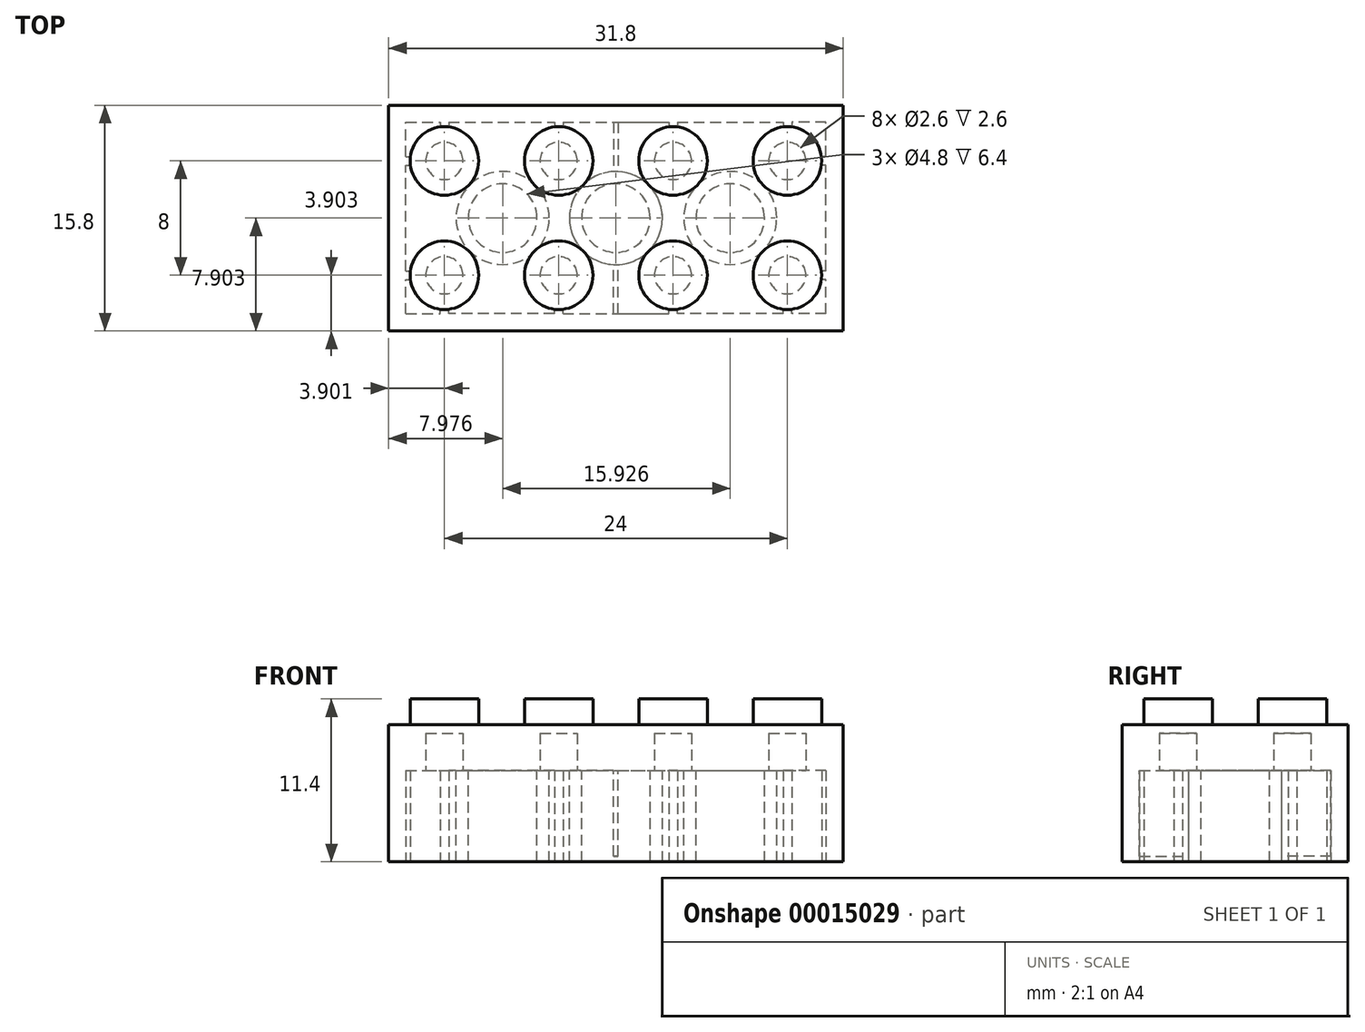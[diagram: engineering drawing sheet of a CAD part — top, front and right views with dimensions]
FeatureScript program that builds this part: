
annotation { "Feature Type Name" : "Feature", "Feature Type Description" : "" }
export const myFeature = defineFeature(function(context is Context, id is Id, definition is map)
    precondition{}
    {
        {
            var Q0;
            Q0=qCreatedBy(makeId("Top.planeOp"),FACE);
            var sketch = newSketch(context, id + "F0", { "sketchPlane" : qUnion([Q0])});
            skLineSegment(sketch, "E0.bottom", {"start": v(-8.05, -0.93) * mm, "end": v(23.75, -0.93) * mm});
            skLineSegment(sketch, "E0.top", {"start": v(-8.05, -16.73) * mm, "end": v(23.75, -16.73) * mm});
            skLineSegment(sketch, "E0.left", {"start": v(-8.05, -0.93) * mm, "end": v(-8.05, -16.73) * mm});
            skLineSegment(sketch, "E0.right", {"start": v(23.75, -0.93) * mm, "end": v(23.75, -16.73) * mm});
            skSolve(sketch);
        }
        {
            var Q0;
            Q0=qCreatedBy(makeId("Top.planeOp"),FACE);
            var sketch = newSketch(context, id + "F1", { "sketchPlane" : qUnion([Q0])});
            skCircle(sketch, "E1", {"center": v(-4.15, -4.83) * mm, "radius": 2.4 * mm});
            skCircle(sketch, "E2", {"center": v(-4.15, -12.83) * mm, "radius": 2.4 * mm});
            skCircle(sketch, "E3", {"center": v(3.85, -4.83) * mm, "radius": 2.4 * mm});
            skCircle(sketch, "E4", {"center": v(3.85, -12.83) * mm, "radius": 2.4 * mm});
            skCircle(sketch, "E5", {"center": v(11.85, -4.83) * mm, "radius": 2.4 * mm});
            skCircle(sketch, "E6", {"center": v(11.85, -12.83) * mm, "radius": 2.4 * mm});
            skCircle(sketch, "E7", {"center": v(19.85, -4.83) * mm, "radius": 2.4 * mm});
            skCircle(sketch, "E8", {"center": v(19.85, -12.83) * mm, "radius": 2.4 * mm});
            skSolve(sketch);
        }
        {
            var Q0;
            Q0=makeQuery(id+"F0.imprint","IMPRINT",FACE,{"disambiguationData":[TD([[makeQuery(id+"F0.imprint","IMPRINT",EDGE,{"derivedFrom":sQuery(id+"F0.wireOp",EDGE,"E0.bottom")}),-1.0]])]});
            extrude(context, id + "F2", {"entities" : qUnion([Q0]), "oppositeDirection" : true, "depth" : 9.6 * mm});
        }
        {
            var Q0;
            Q0=makeQuery(id+"F1.imprint","IMPRINT",FACE,{"disambiguationData":[TD([[makeQuery(id+"F1.imprint","IMPRINT",EDGE,{"derivedFrom":sQuery(id+"F1.wireOp",EDGE,"E1")}),1.0]])]});
            var Q1;
            Q1=makeQuery(id+"F1.imprint","IMPRINT",FACE,{"disambiguationData":[TD([[makeQuery(id+"F1.imprint","IMPRINT",EDGE,{"derivedFrom":sQuery(id+"F1.wireOp",EDGE,"E3")}),1.0]])]});
            var Q2;
            Q2=makeQuery(id+"F1.imprint","IMPRINT",FACE,{"disambiguationData":[TD([[makeQuery(id+"F1.imprint","IMPRINT",EDGE,{"derivedFrom":sQuery(id+"F1.wireOp",EDGE,"E5")}),1.0]])]});
            var Q3;
            Q3=makeQuery(id+"F1.imprint","IMPRINT",FACE,{"disambiguationData":[TD([[makeQuery(id+"F1.imprint","IMPRINT",EDGE,{"derivedFrom":sQuery(id+"F1.wireOp",EDGE,"E7")}),1.0]])]});
            var Q4;
            Q4=makeQuery(id+"F1.imprint","IMPRINT",FACE,{"disambiguationData":[TD([[makeQuery(id+"F1.imprint","IMPRINT",EDGE,{"derivedFrom":sQuery(id+"F1.wireOp",EDGE,"E8")}),1.0]])]});
            var Q5;
            Q5=makeQuery(id+"F1.imprint","IMPRINT",FACE,{"disambiguationData":[TD([[makeQuery(id+"F1.imprint","IMPRINT",EDGE,{"derivedFrom":sQuery(id+"F1.wireOp",EDGE,"E6")}),1.0]])]});
            var Q6;
            Q6=makeQuery(id+"F1.imprint","IMPRINT",FACE,{"disambiguationData":[TD([[makeQuery(id+"F1.imprint","IMPRINT",EDGE,{"derivedFrom":sQuery(id+"F1.wireOp",EDGE,"E4")}),1.0]])]});
            var Q7;
            Q7=makeQuery(id+"F1.imprint","IMPRINT",FACE,{"disambiguationData":[TD([[makeQuery(id+"F1.imprint","IMPRINT",EDGE,{"derivedFrom":sQuery(id+"F1.wireOp",EDGE,"E2")}),1.0]])]});
            extrude(context, id + "F3", {"entities" : qUnion([Q0, Q1, Q2, Q3, Q4, Q5, Q6, Q7]), "operationType" : NewBodyOperationType.ADD, "depth" : 1.8 * mm});
        }
        {
            var Q0;
            Q0=makeQuery(id+"F2.opExtrude","CAP_FACE",FACE,{"disambiguationData":[OSD([sQuery(id+"F0.wireOp",EDGE,"E0.bottom"),sQuery(id+"F0.wireOp",EDGE,"E0.top"),sQuery(id+"F0.wireOp",EDGE,"E0.left"),sQuery(id+"F0.wireOp",EDGE,"E0.right")])],"isStart":false});
            var sketch = newSketch(context, id + "F4", { "sketchPlane" : qUnion([Q0])});
            skLineSegment(sketch, "E9.bottom", {"start": v(-6.85, 15.53) * mm, "end": v(-4.45, 15.53) * mm});
            skLineSegment(sketch, "E9.top", {"start": v(-6.85, 2.13) * mm, "end": v(-4.45, 2.13) * mm});
            skLineSegment(sketch, "E9.left", {"start": v(-6.85, 15.53) * mm, "end": v(-6.85, 13.13) * mm});
            skLineSegment(sketch, "E9.right", {"start": v(22.55, 15.53) * mm, "end": v(22.55, 13.13) * mm});
            skLineSegment(sketch, "E10.rect.bottom", {"start": v(-6.85, 13.13) * mm, "end": v(-6.55, 13.13) * mm});
            skLineSegment(sketch, "E10.rect.top", {"start": v(-6.85, 12.53) * mm, "end": v(-6.55, 12.53) * mm});
            skLineSegment(sketch, "E10.rect.right", {"start": v(-6.55, 13.13) * mm, "end": v(-6.55, 12.53) * mm});
            skPoint(sketch, "E10.rect.middle", {"position": v(-6.7, 12.83) * mm});
            skLineSegment(sketch, "E11.rect.top", {"start": v(-4.45, 15.23) * mm, "end": v(-3.85, 15.23) * mm});
            skLineSegment(sketch, "E11.rect.left", {"start": v(-4.45, 15.53) * mm, "end": v(-4.45, 15.23) * mm});
            skLineSegment(sketch, "E11.rect.right", {"start": v(-3.85, 15.53) * mm, "end": v(-3.85, 15.23) * mm});
            skPoint(sketch, "E11.rect.middle", {"position": v(-4.15, 15.38) * mm});
            skLineSegment(sketch, "E12.rect.top", {"start": v(-4.45, 2.43) * mm, "end": v(-3.85, 2.43) * mm});
            skLineSegment(sketch, "E12.rect.left", {"start": v(-4.45, 2.13) * mm, "end": v(-4.45, 2.43) * mm});
            skLineSegment(sketch, "E12.rect.right", {"start": v(-3.85, 2.13) * mm, "end": v(-3.85, 2.43) * mm});
            skPoint(sketch, "E12.rect.middle", {"position": v(-4.15, 2.28) * mm});
            skLineSegment(sketch, "E13.rect.top", {"start": v(3.55, 2.43) * mm, "end": v(4.15, 2.43) * mm});
            skLineSegment(sketch, "E13.rect.left", {"start": v(3.55, 2.13) * mm, "end": v(3.55, 2.43) * mm});
            skLineSegment(sketch, "E13.rect.right", {"start": v(4.15, 2.13) * mm, "end": v(4.15, 2.43) * mm});
            skPoint(sketch, "E13.rect.middle", {"position": v(3.85, 2.28) * mm});
            skLineSegment(sketch, "E14.rect.top", {"start": v(3.55, 15.23) * mm, "end": v(4.15, 15.23) * mm});
            skLineSegment(sketch, "E14.rect.left", {"start": v(3.55, 15.53) * mm, "end": v(3.55, 15.23) * mm});
            skLineSegment(sketch, "E14.rect.right", {"start": v(4.15, 15.53) * mm, "end": v(4.15, 15.23) * mm});
            skPoint(sketch, "E14.rect.middle", {"position": v(3.85, 15.38) * mm});
            skLineSegment(sketch, "E15.rect.bottom", {"start": v(-6.85, 5.13) * mm, "end": v(-6.55, 5.13) * mm});
            skLineSegment(sketch, "E15.rect.top", {"start": v(-6.85, 4.53) * mm, "end": v(-6.55, 4.53) * mm});
            skLineSegment(sketch, "E15.rect.right", {"start": v(-6.55, 5.13) * mm, "end": v(-6.55, 4.53) * mm});
            skPoint(sketch, "E15.rect.middle", {"position": v(-6.7, 4.83) * mm});
            skLineSegment(sketch, "E16.MirrorCS", {"start": v(20.15, 2.13) * mm, "end": v(20.15, 2.43) * mm});
            skLineSegment(sketch, "E17.MirrorCS", {"start": v(12.15, 2.43) * mm, "end": v(11.55, 2.43) * mm});
            skLineSegment(sketch, "E18.MirrorCS", {"start": v(20.15, 15.23) * mm, "end": v(19.55, 15.23) * mm});
            skLineSegment(sketch, "E19.MirrorCS", {"start": v(22.55, 13.13) * mm, "end": v(22.25, 13.13) * mm});
            skLineSegment(sketch, "E20.MirrorCS", {"start": v(20.15, 2.43) * mm, "end": v(19.55, 2.43) * mm});
            skLineSegment(sketch, "E21.MirrorCS", {"start": v(22.55, 12.53) * mm, "end": v(22.25, 12.53) * mm});
            skLineSegment(sketch, "E22.MirrorCS", {"start": v(22.25, 5.13) * mm, "end": v(22.25, 4.53) * mm});
            skLineSegment(sketch, "E23.MirrorCS", {"start": v(22.55, 4.53) * mm, "end": v(22.25, 4.53) * mm});
            skLineSegment(sketch, "E24.MirrorCS", {"start": v(19.55, 2.13) * mm, "end": v(19.55, 2.43) * mm});
            skLineSegment(sketch, "E25.MirrorCS", {"start": v(12.15, 15.53) * mm, "end": v(12.15, 15.23) * mm});
            skLineSegment(sketch, "E26.MirrorCS", {"start": v(11.55, 15.53) * mm, "end": v(11.55, 15.23) * mm});
            skLineSegment(sketch, "E27.MirrorCS", {"start": v(12.15, 15.23) * mm, "end": v(11.55, 15.23) * mm});
            skLineSegment(sketch, "E28.MirrorCS", {"start": v(11.55, 2.13) * mm, "end": v(11.55, 2.43) * mm});
            skLineSegment(sketch, "E29.MirrorCS", {"start": v(22.55, 5.13) * mm, "end": v(22.25, 5.13) * mm});
            skLineSegment(sketch, "E30.MirrorCS", {"start": v(19.55, 15.53) * mm, "end": v(19.55, 15.23) * mm});
            skLineSegment(sketch, "E31.MirrorCS", {"start": v(20.15, 15.53) * mm, "end": v(20.15, 15.23) * mm});
            skLineSegment(sketch, "E32.MirrorCS", {"start": v(12.15, 2.13) * mm, "end": v(12.15, 2.43) * mm});
            skLineSegment(sketch, "E33.MirrorCS", {"start": v(22.25, 13.13) * mm, "end": v(22.25, 12.53) * mm});
            skLineSegment(sketch, "E34.MirrorCS", {"start": v(22.55, 2.13) * mm, "end": v(20.15, 2.13) * mm});
            skLineSegment(sketch, "E35.MirrorCS", {"start": v(22.55, 15.53) * mm, "end": v(20.15, 15.53) * mm});
            skPoint(sketch, "E36.MirrorP", {"position": v(11.85, 15.38) * mm});
            skPoint(sketch, "E37.MirrorP", {"position": v(19.85, 15.38) * mm});
            skPoint(sketch, "E38.MirrorP", {"position": v(19.85, 2.28) * mm});
            skPoint(sketch, "E39.MirrorP", {"position": v(11.85, 2.28) * mm});
            skPoint(sketch, "E40.MirrorP", {"position": v(22.4, 12.83) * mm});
            skPoint(sketch, "E41.MirrorP", {"position": v(22.4, 4.83) * mm});
            skLineSegment(sketch, "E42.trimOffspring", {"start": v(-6.85, 12.53) * mm, "end": v(-6.85, 5.13) * mm});
            skLineSegment(sketch, "E43.trimOffspring", {"start": v(-6.85, 4.53) * mm, "end": v(-6.85, 2.13) * mm});
            skLineSegment(sketch, "E44.trimOffspring", {"start": v(-3.85, 2.13) * mm, "end": v(3.55, 2.13) * mm});
            skLineSegment(sketch, "E45.trimOffspring", {"start": v(-4.45, 2.13) * mm, "end": v(-6.85, 2.13) * mm});
            skLineSegment(sketch, "E46.trimOffspring", {"start": v(4.15, 2.13) * mm, "end": v(11.55, 2.13) * mm});
            skLineSegment(sketch, "E47.trimOffspring", {"start": v(3.55, 2.13) * mm, "end": v(-3.85, 2.13) * mm});
            skLineSegment(sketch, "E48.trimOffspring", {"start": v(12.15, 2.13) * mm, "end": v(19.55, 2.13) * mm});
            skLineSegment(sketch, "E49.trimOffspring", {"start": v(11.55, 2.13) * mm, "end": v(4.15, 2.13) * mm});
            skLineSegment(sketch, "E50.trimOffspring", {"start": v(19.55, 15.53) * mm, "end": v(12.15, 15.53) * mm});
            skLineSegment(sketch, "E51.trimOffspring", {"start": v(20.15, 15.53) * mm, "end": v(22.55, 15.53) * mm});
            skLineSegment(sketch, "E52.trimOffspring", {"start": v(22.55, 12.53) * mm, "end": v(22.55, 5.13) * mm});
            skLineSegment(sketch, "E53.trimOffspring", {"start": v(22.55, 4.53) * mm, "end": v(22.55, 2.13) * mm});
            skLineSegment(sketch, "E54.trimOffspring", {"start": v(20.15, 2.13) * mm, "end": v(22.55, 2.13) * mm});
            skLineSegment(sketch, "E55.trimOffspring", {"start": v(19.55, 2.13) * mm, "end": v(12.15, 2.13) * mm});
            skLineSegment(sketch, "E56.trimOffspring", {"start": v(3.55, 15.53) * mm, "end": v(-3.85, 15.53) * mm});
            skLineSegment(sketch, "E57.trimOffspring", {"start": v(4.15, 15.53) * mm, "end": v(11.55, 15.53) * mm});
            skLineSegment(sketch, "E58.trimOffspring", {"start": v(-4.45, 15.53) * mm, "end": v(-6.85, 15.53) * mm});
            skLineSegment(sketch, "E59.trimOffspring", {"start": v(-3.85, 15.53) * mm, "end": v(3.55, 15.53) * mm});
            skLineSegment(sketch, "E60.trimOffspring", {"start": v(12.15, 15.53) * mm, "end": v(19.55, 15.53) * mm});
            skLineSegment(sketch, "E61.trimOffspring", {"start": v(11.55, 15.53) * mm, "end": v(4.15, 15.53) * mm});
            skSolve(sketch);
        }
        {
            var Q0;
            Q0=makeQuery(id+"F4.imprint","IMPRINT",FACE,{"disambiguationData":[TD([[makeQuery(id+"F4.imprint","IMPRINT",EDGE,{"derivedFrom":sQuery(id+"F4.wireOp",EDGE,"E9.left")}),1.0]])]});
            extrude(context, id + "F5", {"entities" : qUnion([Q0]), "operationType" : NewBodyOperationType.REMOVE, "oppositeDirection" : true, "depth" : 6.4 * mm});
        }
        {
            var Q0;
            Q0=makeQuery(id+"F5.boolean.opBoolean","COPY",FACE,{"derivedFrom":makeQuery(id+"F5.opExtrude","CAP_FACE",FACE,{"disambiguationData":[OSD([sQuery(id+"F4.wireOp",EDGE,"E9.left"),sQuery(id+"F4.wireOp",EDGE,"E10.rect.bottom"),sQuery(id+"F4.wireOp",EDGE,"E10.rect.top"),sQuery(id+"F4.wireOp",EDGE,"E10.rect.right"),sQuery(id+"F4.wireOp",EDGE,"E11.rect.top"),sQuery(id+"F4.wireOp",EDGE,"E11.rect.left"),sQuery(id+"F4.wireOp",EDGE,"E11.rect.right"),sQuery(id+"F4.wireOp",EDGE,"E12.rect.top"),sQuery(id+"F4.wireOp",EDGE,"E12.rect.left"),sQuery(id+"F4.wireOp",EDGE,"E12.rect.right"),sQuery(id+"F4.wireOp",EDGE,"E13.rect.top"),sQuery(id+"F4.wireOp",EDGE,"E13.rect.left"),sQuery(id+"F4.wireOp",EDGE,"E13.rect.right"),sQuery(id+"F4.wireOp",EDGE,"E14.rect.top"),sQuery(id+"F4.wireOp",EDGE,"E14.rect.left"),sQuery(id+"F4.wireOp",EDGE,"E14.rect.right"),sQuery(id+"F4.wireOp",EDGE,"E15.rect.bottom"),sQuery(id+"F4.wireOp",EDGE,"E15.rect.top"),sQuery(id+"F4.wireOp",EDGE,"E15.rect.right"),sQuery(id+"F4.wireOp",EDGE,"E16.MirrorCS"),sQuery(id+"F4.wireOp",EDGE,"E17.MirrorCS"),sQuery(id+"F4.wireOp",EDGE,"E18.MirrorCS"),sQuery(id+"F4.wireOp",EDGE,"E19.MirrorCS"),sQuery(id+"F4.wireOp",EDGE,"E20.MirrorCS"),sQuery(id+"F4.wireOp",EDGE,"E21.MirrorCS"),sQuery(id+"F4.wireOp",EDGE,"E22.MirrorCS"),sQuery(id+"F4.wireOp",EDGE,"E23.MirrorCS"),sQuery(id+"F4.wireOp",EDGE,"E24.MirrorCS"),sQuery(id+"F4.wireOp",EDGE,"E25.MirrorCS"),sQuery(id+"F4.wireOp",EDGE,"E26.MirrorCS"),sQuery(id+"F4.wireOp",EDGE,"E27.MirrorCS"),sQuery(id+"F4.wireOp",EDGE,"E28.MirrorCS"),sQuery(id+"F4.wireOp",EDGE,"E29.MirrorCS"),sQuery(id+"F4.wireOp",EDGE,"E30.MirrorCS"),sQuery(id+"F4.wireOp",EDGE,"E31.MirrorCS"),sQuery(id+"F4.wireOp",EDGE,"E32.MirrorCS"),sQuery(id+"F4.wireOp",EDGE,"E33.MirrorCS"),sQuery(id+"F4.wireOp",EDGE,"E9.right"),sQuery(id+"F4.wireOp",EDGE,"E42.trimOffspring"),sQuery(id+"F4.wireOp",EDGE,"E43.trimOffspring"),sQuery(id+"F4.wireOp",EDGE,"E45.trimOffspring"),sQuery(id+"F4.wireOp",EDGE,"E47.trimOffspring"),sQuery(id+"F4.wireOp",EDGE,"E49.trimOffspring"),sQuery(id+"F4.wireOp",EDGE,"E51.trimOffspring"),sQuery(id+"F4.wireOp",EDGE,"E52.trimOffspring"),sQuery(id+"F4.wireOp",EDGE,"E53.trimOffspring"),sQuery(id+"F4.wireOp",EDGE,"E54.trimOffspring"),sQuery(id+"F4.wireOp",EDGE,"E55.trimOffspring"),sQuery(id+"F4.wireOp",EDGE,"E58.trimOffspring"),sQuery(id+"F4.wireOp",EDGE,"E59.trimOffspring"),sQuery(id+"F4.wireOp",EDGE,"E60.trimOffspring"),sQuery(id+"F4.wireOp",EDGE,"E61.trimOffspring")])],"isStart":false})});
            var sketch = newSketch(context, id + "F6", { "sketchPlane" : qUnion([Q0])});
            skLineSegment(sketch, "E62", {"start": v(-6.55, 12.83) * mm, "end": v(22.25, 12.83) * mm, "construction": true});
            skLineSegment(sketch, "E63", {"start": v(19.85, 15.23) * mm, "end": v(19.85, 2.43) * mm, "construction": true});
            skLineSegment(sketch, "E64", {"start": v(11.85, 15.23) * mm, "end": v(11.85, 2.43) * mm, "construction": true});
            skLineSegment(sketch, "E65", {"start": v(3.85, 2.43) * mm, "end": v(3.85, 15.23) * mm, "construction": true});
            skLineSegment(sketch, "E66", {"start": v(-4.15, 15.23) * mm, "end": v(-4.15, 2.43) * mm, "construction": true});
            skLineSegment(sketch, "E67", {"start": v(-6.55, 4.83) * mm, "end": v(22.25, 4.83) * mm, "construction": true});
            skCircle(sketch, "E68", {"center": v(-4.15, 12.83) * mm, "radius": 1.3 * mm});
            skCircle(sketch, "E69", {"center": v(-4.15, 4.83) * mm, "radius": 1.3 * mm});
            skCircle(sketch, "E70", {"center": v(3.85, 4.83) * mm, "radius": 1.3 * mm});
            skCircle(sketch, "E71", {"center": v(3.85, 12.83) * mm, "radius": 1.3 * mm});
            skCircle(sketch, "E72", {"center": v(11.85, 12.83) * mm, "radius": 1.3 * mm});
            skCircle(sketch, "E73", {"center": v(19.85, 12.83) * mm, "radius": 1.3 * mm});
            skCircle(sketch, "E74", {"center": v(19.85, 4.83) * mm, "radius": 1.3 * mm});
            skCircle(sketch, "E75", {"center": v(11.85, 4.83) * mm, "radius": 1.3 * mm});
            skSolve(sketch);
        }
        {
            var Q0;
            Q0=makeQuery(id+"F6.imprint","IMPRINT",FACE,{"disambiguationData":[TD([[makeQuery(id+"F6.imprint","IMPRINT",EDGE,{"derivedFrom":sQuery(id+"F6.wireOp",EDGE,"E68")}),1.0]])]});
            var Q1;
            Q1=makeQuery(id+"F6.imprint","IMPRINT",FACE,{"disambiguationData":[TD([[makeQuery(id+"F6.imprint","IMPRINT",EDGE,{"derivedFrom":sQuery(id+"F6.wireOp",EDGE,"E71")}),1.0]])]});
            var Q2;
            Q2=makeQuery(id+"F6.imprint","IMPRINT",FACE,{"disambiguationData":[TD([[makeQuery(id+"F6.imprint","IMPRINT",EDGE,{"derivedFrom":sQuery(id+"F6.wireOp",EDGE,"E72")}),1.0]])]});
            var Q3;
            Q3=makeQuery(id+"F6.imprint","IMPRINT",FACE,{"disambiguationData":[TD([[makeQuery(id+"F6.imprint","IMPRINT",EDGE,{"derivedFrom":sQuery(id+"F6.wireOp",EDGE,"E73")}),1.0]])]});
            var Q4;
            Q4=makeQuery(id+"F6.imprint","IMPRINT",FACE,{"disambiguationData":[TD([[makeQuery(id+"F6.imprint","IMPRINT",EDGE,{"derivedFrom":sQuery(id+"F6.wireOp",EDGE,"E74")}),1.0]])]});
            var Q5;
            Q5=makeQuery(id+"F6.imprint","IMPRINT",FACE,{"disambiguationData":[TD([[makeQuery(id+"F6.imprint","IMPRINT",EDGE,{"derivedFrom":sQuery(id+"F6.wireOp",EDGE,"E75")}),1.0]])]});
            var Q6;
            Q6=makeQuery(id+"F6.imprint","IMPRINT",FACE,{"disambiguationData":[TD([[makeQuery(id+"F6.imprint","IMPRINT",EDGE,{"derivedFrom":sQuery(id+"F6.wireOp",EDGE,"E70")}),1.0]])]});
            var Q7;
            Q7=makeQuery(id+"F6.imprint","IMPRINT",FACE,{"disambiguationData":[TD([[makeQuery(id+"F6.imprint","IMPRINT",EDGE,{"derivedFrom":sQuery(id+"F6.wireOp",EDGE,"E69")}),1.0]])]});
            extrude(context, id + "F7", {"entities" : qUnion([Q0, Q1, Q2, Q3, Q4, Q5, Q6, Q7]), "operationType" : NewBodyOperationType.REMOVE, "oppositeDirection" : true, "depth" : 2.6 * mm});
        }
        {
            var Q0;
            Q0=makeQuery(id+"F5.boolean.opBoolean","COPY",FACE,{"derivedFrom":makeQuery(id+"F5.opExtrude","CAP_FACE",FACE,{"disambiguationData":[OSD([sQuery(id+"F4.wireOp",EDGE,"E9.left"),sQuery(id+"F4.wireOp",EDGE,"E10.rect.bottom"),sQuery(id+"F4.wireOp",EDGE,"E10.rect.top"),sQuery(id+"F4.wireOp",EDGE,"E10.rect.right"),sQuery(id+"F4.wireOp",EDGE,"E11.rect.top"),sQuery(id+"F4.wireOp",EDGE,"E11.rect.left"),sQuery(id+"F4.wireOp",EDGE,"E11.rect.right"),sQuery(id+"F4.wireOp",EDGE,"E12.rect.top"),sQuery(id+"F4.wireOp",EDGE,"E12.rect.left"),sQuery(id+"F4.wireOp",EDGE,"E12.rect.right"),sQuery(id+"F4.wireOp",EDGE,"E13.rect.top"),sQuery(id+"F4.wireOp",EDGE,"E13.rect.left"),sQuery(id+"F4.wireOp",EDGE,"E13.rect.right"),sQuery(id+"F4.wireOp",EDGE,"E14.rect.top"),sQuery(id+"F4.wireOp",EDGE,"E14.rect.left"),sQuery(id+"F4.wireOp",EDGE,"E14.rect.right"),sQuery(id+"F4.wireOp",EDGE,"E15.rect.bottom"),sQuery(id+"F4.wireOp",EDGE,"E15.rect.top"),sQuery(id+"F4.wireOp",EDGE,"E15.rect.right"),sQuery(id+"F4.wireOp",EDGE,"E16.MirrorCS"),sQuery(id+"F4.wireOp",EDGE,"E17.MirrorCS"),sQuery(id+"F4.wireOp",EDGE,"E18.MirrorCS"),sQuery(id+"F4.wireOp",EDGE,"E19.MirrorCS"),sQuery(id+"F4.wireOp",EDGE,"E20.MirrorCS"),sQuery(id+"F4.wireOp",EDGE,"E21.MirrorCS"),sQuery(id+"F4.wireOp",EDGE,"E22.MirrorCS"),sQuery(id+"F4.wireOp",EDGE,"E23.MirrorCS"),sQuery(id+"F4.wireOp",EDGE,"E24.MirrorCS"),sQuery(id+"F4.wireOp",EDGE,"E25.MirrorCS"),sQuery(id+"F4.wireOp",EDGE,"E26.MirrorCS"),sQuery(id+"F4.wireOp",EDGE,"E27.MirrorCS"),sQuery(id+"F4.wireOp",EDGE,"E28.MirrorCS"),sQuery(id+"F4.wireOp",EDGE,"E29.MirrorCS"),sQuery(id+"F4.wireOp",EDGE,"E30.MirrorCS"),sQuery(id+"F4.wireOp",EDGE,"E31.MirrorCS"),sQuery(id+"F4.wireOp",EDGE,"E32.MirrorCS"),sQuery(id+"F4.wireOp",EDGE,"E33.MirrorCS"),sQuery(id+"F4.wireOp",EDGE,"E9.right"),sQuery(id+"F4.wireOp",EDGE,"E42.trimOffspring"),sQuery(id+"F4.wireOp",EDGE,"E43.trimOffspring"),sQuery(id+"F4.wireOp",EDGE,"E45.trimOffspring"),sQuery(id+"F4.wireOp",EDGE,"E47.trimOffspring"),sQuery(id+"F4.wireOp",EDGE,"E49.trimOffspring"),sQuery(id+"F4.wireOp",EDGE,"E51.trimOffspring"),sQuery(id+"F4.wireOp",EDGE,"E52.trimOffspring"),sQuery(id+"F4.wireOp",EDGE,"E53.trimOffspring"),sQuery(id+"F4.wireOp",EDGE,"E54.trimOffspring"),sQuery(id+"F4.wireOp",EDGE,"E55.trimOffspring"),sQuery(id+"F4.wireOp",EDGE,"E58.trimOffspring"),sQuery(id+"F4.wireOp",EDGE,"E59.trimOffspring"),sQuery(id+"F4.wireOp",EDGE,"E60.trimOffspring"),sQuery(id+"F4.wireOp",EDGE,"E61.trimOffspring")])],"isStart":false})});
            var sketch = newSketch(context, id + "F8", { "sketchPlane" : qUnion([Q0])});
            skLineSegment(sketch, "E76", {"start": v(-6.85, 8.83) * mm, "end": v(22.55, 8.83) * mm, "construction": true});
            skLineSegment(sketch, "E77", {"start": v(7.85, 15.53) * mm, "end": v(7.85, 2.13) * mm, "construction": true});
            skLineSegment(sketch, "E78", {"start": v(-0.15, 15.53) * mm, "end": v(0, 2.13) * mm, "construction": true});
            skLineSegment(sketch, "E79", {"start": v(15.85, 15.53) * mm, "end": v(15.85, 2.13) * mm, "construction": true});
            skCircle(sketch, "E80", {"center": v(-0.07, 8.83) * mm, "radius": 2.4 * mm});
            skCircle(sketch, "E81", {"center": v(7.85, 8.83) * mm, "radius": 2.4 * mm});
            skCircle(sketch, "E82", {"center": v(15.85, 8.83) * mm, "radius": 2.4 * mm});
            skCircle(sketch, "E83", {"center": v(-0.07, 8.83) * mm, "radius": 3.26 * mm});
            skCircle(sketch, "E84", {"center": v(7.85, 8.83) * mm, "radius": 3.26 * mm});
            skCircle(sketch, "E85", {"center": v(15.85, 8.83) * mm, "radius": 3.26 * mm});
            skSolve(sketch);
        }
        {
            var Q0;
            Q0=makeQuery(id+"F8.imprint","IMPRINT",FACE,{"disambiguationData":[TD([[makeQuery(id+"F8.imprint","IMPRINT",EDGE,{"derivedFrom":sQuery(id+"F8.wireOp",EDGE,"E80")}),-1.0]])]});
            var Q1;
            Q1=makeQuery(id+"F8.imprint","IMPRINT",FACE,{"disambiguationData":[TD([[makeQuery(id+"F8.imprint","IMPRINT",EDGE,{"derivedFrom":sQuery(id+"F8.wireOp",EDGE,"E81")}),-1.0]])]});
            var Q2;
            Q2=makeQuery(id+"F8.imprint","IMPRINT",FACE,{"disambiguationData":[TD([[makeQuery(id+"F8.imprint","IMPRINT",EDGE,{"derivedFrom":sQuery(id+"F8.wireOp",EDGE,"E82")}),-1.0]])]});
            extrude(context, id + "F9", {"entities" : qUnion([Q0, Q1, Q2]), "operationType" : NewBodyOperationType.ADD, "depth" : 6.4 * mm});
        }
        {
            var Q0;
            {var subQ0=sQuery(id+"F4.wireOp",EDGE,"E9.left");var subQ1=sQuery(id+"F4.wireOp",EDGE,"E10.rect.bottom");var subQ2=sQuery(id+"F4.wireOp",EDGE,"E10.rect.top");var subQ3=sQuery(id+"F4.wireOp",EDGE,"E10.rect.right");var subQ4=sQuery(id+"F4.wireOp",EDGE,"E11.rect.top");var subQ5=sQuery(id+"F4.wireOp",EDGE,"E11.rect.left");var subQ6=sQuery(id+"F4.wireOp",EDGE,"E11.rect.right");var subQ7=sQuery(id+"F4.wireOp",EDGE,"E12.rect.top");var subQ8=sQuery(id+"F4.wireOp",EDGE,"E12.rect.left");var subQ9=sQuery(id+"F4.wireOp",EDGE,"E12.rect.right");var subQ10=sQuery(id+"F4.wireOp",EDGE,"E13.rect.top");var subQ11=sQuery(id+"F4.wireOp",EDGE,"E13.rect.left");var subQ12=sQuery(id+"F4.wireOp",EDGE,"E13.rect.right");var subQ13=sQuery(id+"F4.wireOp",EDGE,"E14.rect.top");var subQ14=sQuery(id+"F4.wireOp",EDGE,"E14.rect.left");var subQ15=sQuery(id+"F4.wireOp",EDGE,"E14.rect.right");var subQ16=sQuery(id+"F4.wireOp",EDGE,"E15.rect.bottom");var subQ17=sQuery(id+"F4.wireOp",EDGE,"E15.rect.top");var subQ18=sQuery(id+"F4.wireOp",EDGE,"E15.rect.right");var subQ19=sQuery(id+"F4.wireOp",EDGE,"E16.MirrorCS");var subQ20=sQuery(id+"F4.wireOp",EDGE,"E17.MirrorCS");var subQ21=sQuery(id+"F4.wireOp",EDGE,"E18.MirrorCS");var subQ22=sQuery(id+"F4.wireOp",EDGE,"E19.MirrorCS");var subQ23=sQuery(id+"F4.wireOp",EDGE,"E20.MirrorCS");var subQ24=sQuery(id+"F4.wireOp",EDGE,"E21.MirrorCS");var subQ25=sQuery(id+"F4.wireOp",EDGE,"E22.MirrorCS");var subQ26=sQuery(id+"F4.wireOp",EDGE,"E23.MirrorCS");var subQ27=sQuery(id+"F4.wireOp",EDGE,"E24.MirrorCS");var subQ28=sQuery(id+"F4.wireOp",EDGE,"E25.MirrorCS");var subQ29=sQuery(id+"F4.wireOp",EDGE,"E26.MirrorCS");var subQ30=sQuery(id+"F4.wireOp",EDGE,"E27.MirrorCS");var subQ31=sQuery(id+"F4.wireOp",EDGE,"E28.MirrorCS");var subQ32=sQuery(id+"F4.wireOp",EDGE,"E29.MirrorCS");var subQ33=sQuery(id+"F4.wireOp",EDGE,"E30.MirrorCS");var subQ34=sQuery(id+"F4.wireOp",EDGE,"E31.MirrorCS");var subQ35=sQuery(id+"F4.wireOp",EDGE,"E32.MirrorCS");var subQ36=sQuery(id+"F4.wireOp",EDGE,"E33.MirrorCS");var subQ37=sQuery(id+"F4.wireOp",EDGE,"E9.right");var subQ38=sQuery(id+"F4.wireOp",EDGE,"E42.trimOffspring");var subQ39=sQuery(id+"F4.wireOp",EDGE,"E43.trimOffspring");var subQ40=sQuery(id+"F4.wireOp",EDGE,"E45.trimOffspring");var subQ41=sQuery(id+"F4.wireOp",EDGE,"E47.trimOffspring");var subQ42=sQuery(id+"F4.wireOp",EDGE,"E49.trimOffspring");var subQ43=sQuery(id+"F4.wireOp",EDGE,"E51.trimOffspring");var subQ44=sQuery(id+"F4.wireOp",EDGE,"E52.trimOffspring");var subQ45=sQuery(id+"F4.wireOp",EDGE,"E53.trimOffspring");var subQ46=sQuery(id+"F4.wireOp",EDGE,"E54.trimOffspring");var subQ47=sQuery(id+"F4.wireOp",EDGE,"E55.trimOffspring");var subQ48=sQuery(id+"F4.wireOp",EDGE,"E58.trimOffspring");var subQ49=sQuery(id+"F4.wireOp",EDGE,"E59.trimOffspring");var subQ50=sQuery(id+"F4.wireOp",EDGE,"E60.trimOffspring");var subQ51=sQuery(id+"F4.wireOp",EDGE,"E61.trimOffspring");Q0=makeQuery(id+"F9.boolean.opBoolean","SPLIT",FACE,{"disambiguationData":[TD([makeQuery(id+"F5.boolean.opBoolean","COPY",FACE,{"derivedFrom":makeQuery(id+"F5.opExtrude","SWEPT_FACE",FACE,{"disambiguationData":[OSD([subQ0])]})})])],"derivedFrom":makeQuery(id+"F5.boolean.opBoolean","COPY",FACE,{"derivedFrom":makeQuery(id+"F5.opExtrude","CAP_FACE",FACE,{"disambiguationData":[OSD([subQ0,subQ1,subQ2,subQ3,subQ4,subQ5,subQ6,subQ7,subQ8,subQ9,subQ10,subQ11,subQ12,subQ13,subQ14,subQ15,subQ16,subQ17,subQ18,subQ19,subQ20,subQ21,subQ22,subQ23,subQ24,subQ25,subQ26,subQ27,subQ28,subQ29,subQ30,subQ31,subQ32,subQ33,subQ34,subQ35,subQ36,subQ37,subQ38,subQ39,subQ40,subQ41,subQ42,subQ43,subQ44,subQ45,subQ46,subQ47,subQ48,subQ49,subQ50,subQ51])],"isStart":false})})});}
            var sketch = newSketch(context, id + "F10", { "sketchPlane" : qUnion([Q0])});
            skLineSegment(sketch, "E86.rect.bottom", {"start": v(7.7, 15.53) * mm, "end": v(8, 15.53) * mm, "construction": true});
            skLineSegment(sketch, "E86.rect.right", {"start": v(8, 15.53) * mm, "end": v(8, 12.17) * mm, "construction": true});
            skLineSegment(sketch, "E87", {"start": v(7.7, 15.53) * mm, "end": v(7.7, 12.08) * mm});
            skLineSegment(sketch, "E88", {"start": v(8, 15.53) * mm, "end": v(8, 12.08) * mm});
            skLineSegment(sketch, "E89", {"start": v(7.7, 2.13) * mm, "end": v(7.7, 5.57) * mm});
            skLineSegment(sketch, "E90", {"start": v(8, 2.13) * mm, "end": v(8, 5.57) * mm});
            skSolve(sketch);
        }
        {
            var Q0;
            {var subQ2=sQuery(id+"F10.wireOp",EDGE,"E87");Q0=makeQuery(id+"F10.imprint","IMPRINT",FACE,{"disambiguationData":[TD([[makeQuery(id+"F10.imprint","IMPRINT",EDGE,{"derivedFrom":subQ2}),1.0]])]});}
            var Q1;
            {var subQ2=sQuery(id+"F10.wireOp",EDGE,"E89");Q1=makeQuery(id+"F10.imprint","IMPRINT",FACE,{"disambiguationData":[TD([[makeQuery(id+"F10.imprint","IMPRINT",EDGE,{"derivedFrom":subQ2}),-1.0]])]});}
            extrude(context, id + "F11", {"entities" : qUnion([Q0, Q1]), "operationType" : NewBodyOperationType.ADD, "depth" : 6 * mm});
        }
    });
